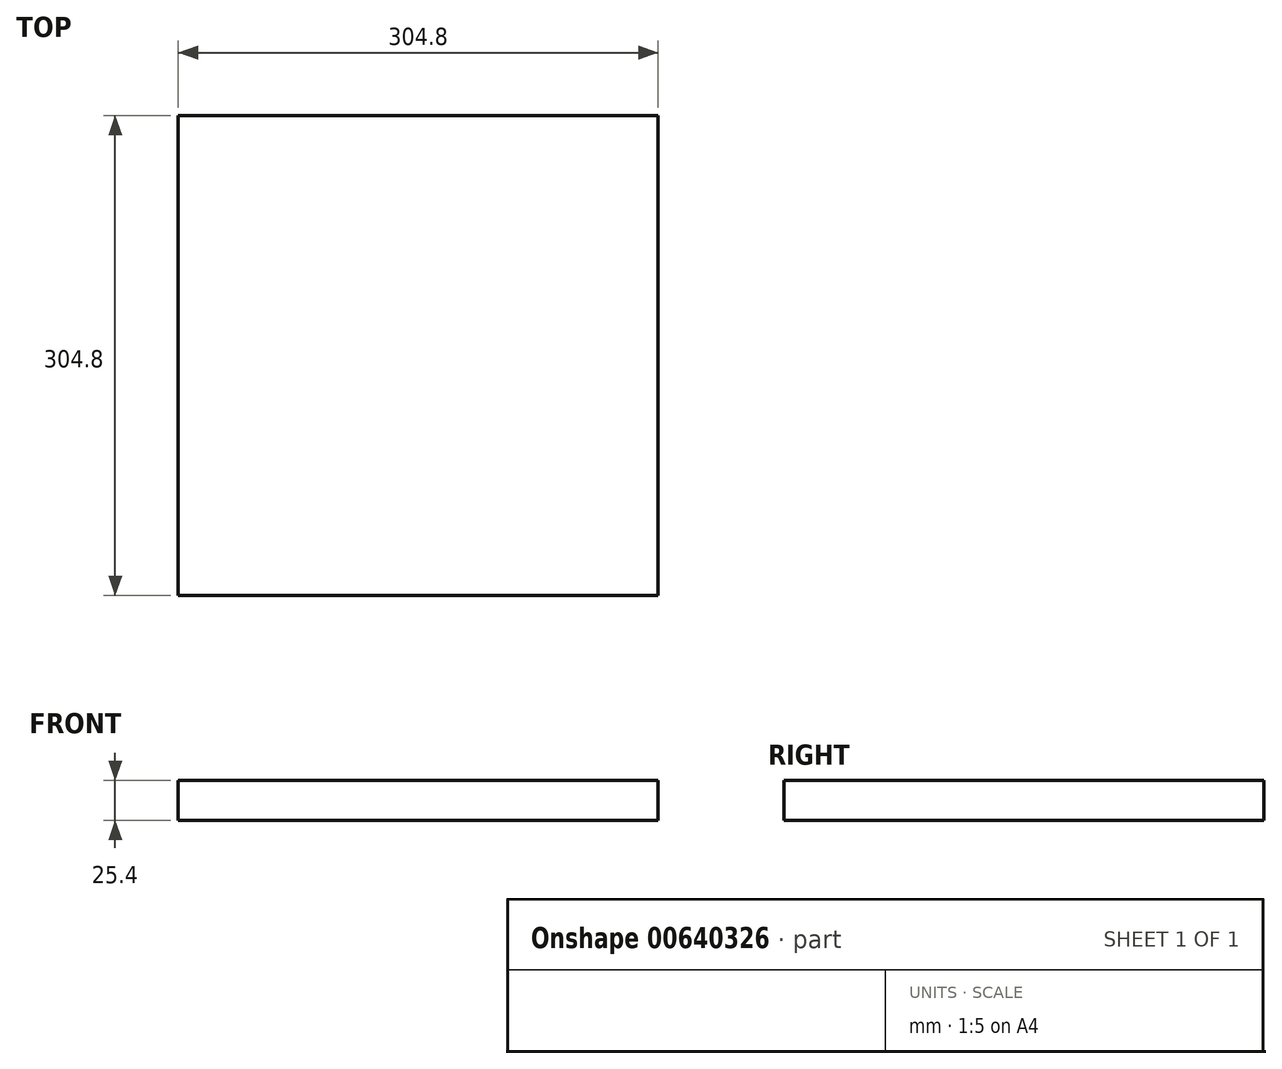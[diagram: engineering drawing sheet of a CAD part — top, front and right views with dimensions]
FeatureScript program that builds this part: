
annotation { "Feature Type Name" : "Feature", "Feature Type Description" : "" }
export const myFeature = defineFeature(function(context is Context, id is Id, definition is map)
    precondition{}
    {
        {
            var Q0;
            Q0=qCreatedBy(makeId("Top.planeOp"),FACE);
            var sketch = newSketch(context, id + "F0", { "sketchPlane" : qUnion([Q0])});
            skLineSegment(sketch, "E0.bottom", {"start": v(-128.7, 220.6) * mm, "end": v(176.1, 220.6) * mm});
            skLineSegment(sketch, "E0.top", {"start": v(-128.7, -84.2) * mm, "end": v(176.1, -84.2) * mm});
            skLineSegment(sketch, "E0.left", {"start": v(-128.7, 220.6) * mm, "end": v(-128.7, -84.2) * mm});
            skLineSegment(sketch, "E0.right", {"start": v(176.1, 220.6) * mm, "end": v(176.1, -84.2) * mm});
            skSolve(sketch);
        }
        {
            var Q0;
            Q0 = qSketchRegion(id + "F0", true);
            extrude(context, id + "F1", {"entities" : qUnion([Q0]), "depth" : 25.4 * mm, "offsetDistance" : 25.4 * mm});
        }
    });
